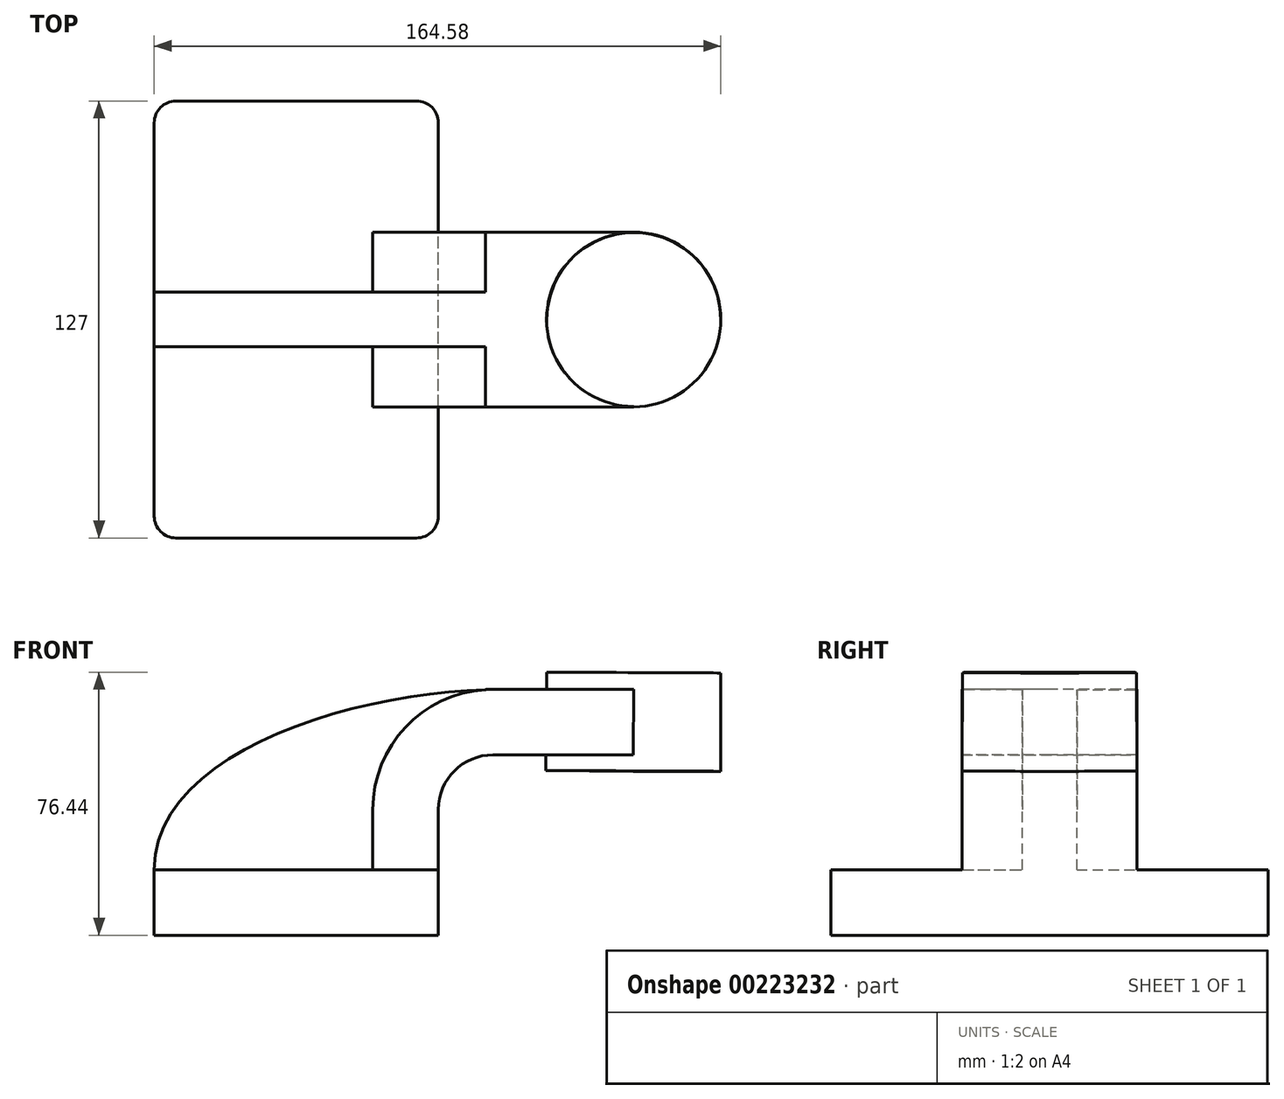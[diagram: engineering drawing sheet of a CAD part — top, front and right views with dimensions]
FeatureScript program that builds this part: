
annotation { "Feature Type Name" : "Feature", "Feature Type Description" : "" }
export const myFeature = defineFeature(function(context is Context, id is Id, definition is map)
    precondition{}
    {
        {
            var Q0;
            Q0=qCreatedBy(makeId("Front.planeOp"),FACE);
            var sketch = newSketch(context, id + "F0", { "sketchPlane" : qUnion([Q0])});
            skLineSegment(sketch, "E0.bottom", {"start": v(-41.27, -9.53) * mm, "end": v(41.28, -9.53) * mm});
            skLineSegment(sketch, "E0.top", {"start": v(-41.28, 9.52) * mm, "end": v(41.28, 9.52) * mm});
            skLineSegment(sketch, "E0.left", {"start": v(-41.28, -9.53) * mm, "end": v(-41.28, 9.52) * mm});
            skLineSegment(sketch, "E0.right", {"start": v(41.28, -9.53) * mm, "end": v(41.28, 9.52) * mm});
            skPoint(sketch, "E0.middle", {"position": v(0, 0) * mm});
            skLineSegment(sketch, "E1.bottom", {"start": v(72.5, 38.1) * mm, "end": v(123.3, 38.1) * mm});
            skLineSegment(sketch, "E1.top", {"start": v(72.5, 66.67) * mm, "end": v(123.3, 66.67) * mm});
            skLineSegment(sketch, "E1.left", {"start": v(72.5, 38.1) * mm, "end": v(72.5, 66.67) * mm});
            skLineSegment(sketch, "E1.right", {"start": v(123.3, 38.1) * mm, "end": v(123.3, 66.67) * mm});
            skPoint(sketch, "E1.middle", {"position": v(97.9, 52.39) * mm});
            skLineSegment(sketch, "E2", {"start": v(41.27, 9.52) * mm, "end": v(41.27, 27) * mm});
            skArc(sketch, "E3", {"start": v(41.27, 27) * mm, "mid": v(45.92, 38.23) * mm, "end": v(57.15, 42.88) * mm});
            skLineSegment(sketch, "E4", {"start": v(57.15, 42.88) * mm, "end": v(98.38, 42.88) * mm});
            skLineSegment(sketch, "E5.0", {"start": v(57.15, 61.93) * mm, "end": v(98.03, 61.93) * mm});
            skArc(sketch, "E5.1", {"start": v(22.22, 27) * mm, "mid": v(32.45, 51.7) * mm, "end": v(57.15, 61.93) * mm});
            skLineSegment(sketch, "E5.2", {"start": v(22.22, 9.52) * mm, "end": v(22.22, 27) * mm});
            skFitSpline(sketch, "E6", {"points": [v(-41.27, 9.52) * mm, v(59.15, 61.93) * mm], "startDerivative": vector(0.38, 105.82) * mm, "endDerivative": vector(117.9, 0.26) * mm});
            skLineSegment(sketch, "E7", {"start": v(97.9, 38.1) * mm, "end": v(98.03, 66.67) * mm});
            skSolve(sketch);
        }
        {
            var Q0;
            Q0=makeQuery(id+"F0.imprint","IMPRINT",FACE,{"disambiguationData":[TD([[makeQuery(id+"F0.imprint","IMPRINT",EDGE,{"derivedFrom":sQuery(id+"F0.wireOp",EDGE,"E0.bottom")}),1.0]])]});
            extrude(context, id + "F1", {"entities" : qUnion([Q0]), "endBound" : BoundingType.SYMMETRIC, "depth" : 127 * mm});
        }
        {
            var Q0;
            {var subQ3=sQuery(id+"F0.wireOp",EDGE,"E5.2");Q0=makeQuery(id+"F0.imprint","IMPRINT",FACE,{"disambiguationData":[TD([[makeQuery(id+"F0.imprint","IMPRINT",EDGE,{"derivedFrom":subQ3}),1.0]])]});}
            extrude(context, id + "F2", {"entities" : qUnion([Q0]), "operationType" : NewBodyOperationType.ADD, "endBound" : BoundingType.SYMMETRIC, "depth" : 15.88 * mm});
        }
        {
            var Q0;
            {var subQ0=sQuery(id+"F0.wireOp",EDGE,"E4");var subQ1=sQuery(id+"F0.wireOp",EDGE,"E1.left");var subQ2=makeQuery(id+"F0.imprint","INTERSECT",VERTEX,{"derivedFrom":[subQ1,subQ0]});Q0=makeQuery(id+"F0.imprint","IMPRINT",FACE,{"disambiguationData":[TD([[makeQuery(id+"F0.imprint","IMPRINT",EDGE,{"disambiguationData":[TD([[subQ2,-1.0]])],"derivedFrom":subQ1}),-1.0]])]});}
            var Q1;
            {var subQ6=sQuery(id+"F0.wireOp",EDGE,"E2");Q1=makeQuery(id+"F0.imprint","IMPRINT",FACE,{"disambiguationData":[TD([[makeQuery(id+"F0.imprint","IMPRINT",EDGE,{"derivedFrom":subQ6}),1.0]])]});}
            extrude(context, id + "F3", {"entities" : qUnion([Q0, Q1]), "operationType" : NewBodyOperationType.ADD, "endBound" : BoundingType.SYMMETRIC, "depth" : 50.8 * mm});
        }
        {
            var Q0;
            {var subQ0=sQuery(id+"F0.wireOp",EDGE,"E1.right");Q0=makeQuery(id+"F0.imprint","IMPRINT",FACE,{"disambiguationData":[TD([[makeQuery(id+"F0.imprint","IMPRINT",EDGE,{"derivedFrom":subQ0}),1.0]])]});}
            var Q1;
            Q1=sQuery(id+"F0.wireOp",EDGE,"E7");
            revolve(context, id + "F4", {"operationType" : NewBodyOperationType.ADD, "entities" : qUnion([Q0]), "axis" : qUnion([Q1]), "revolveType" : RevolveType.FULL});
        }
        {
            var Q0;
            Q0=makeQuery(id+"F1.opExtrude","CAP_EDGE",EDGE,{"disambiguationData":[OSD([sQuery(id+"F0.wireOp",EDGE,"E0.left")])],"isStart":false});
            var Q1;
            Q1=makeQuery(id+"F1.opExtrude","CAP_EDGE",EDGE,{"disambiguationData":[OSD([sQuery(id+"F0.wireOp",EDGE,"E0.right")])],"isStart":false});
            var Q2;
            Q2=makeQuery(id+"F1.opExtrude","CAP_EDGE",EDGE,{"disambiguationData":[OSD([sQuery(id+"F0.wireOp",EDGE,"E0.right")])],"isStart":true});
            var Q3;
            Q3=makeQuery(id+"F1.opExtrude","CAP_EDGE",EDGE,{"disambiguationData":[OSD([sQuery(id+"F0.wireOp",EDGE,"E0.left")])],"isStart":true});
            fillet(context, id + "F5", {"entities" : qUnion([Q0, Q1, Q2, Q3]), "radius" : 6.35 * mm, "tangentPropagation" : true, "allowEdgeOverflow" : false});
        }
    });
